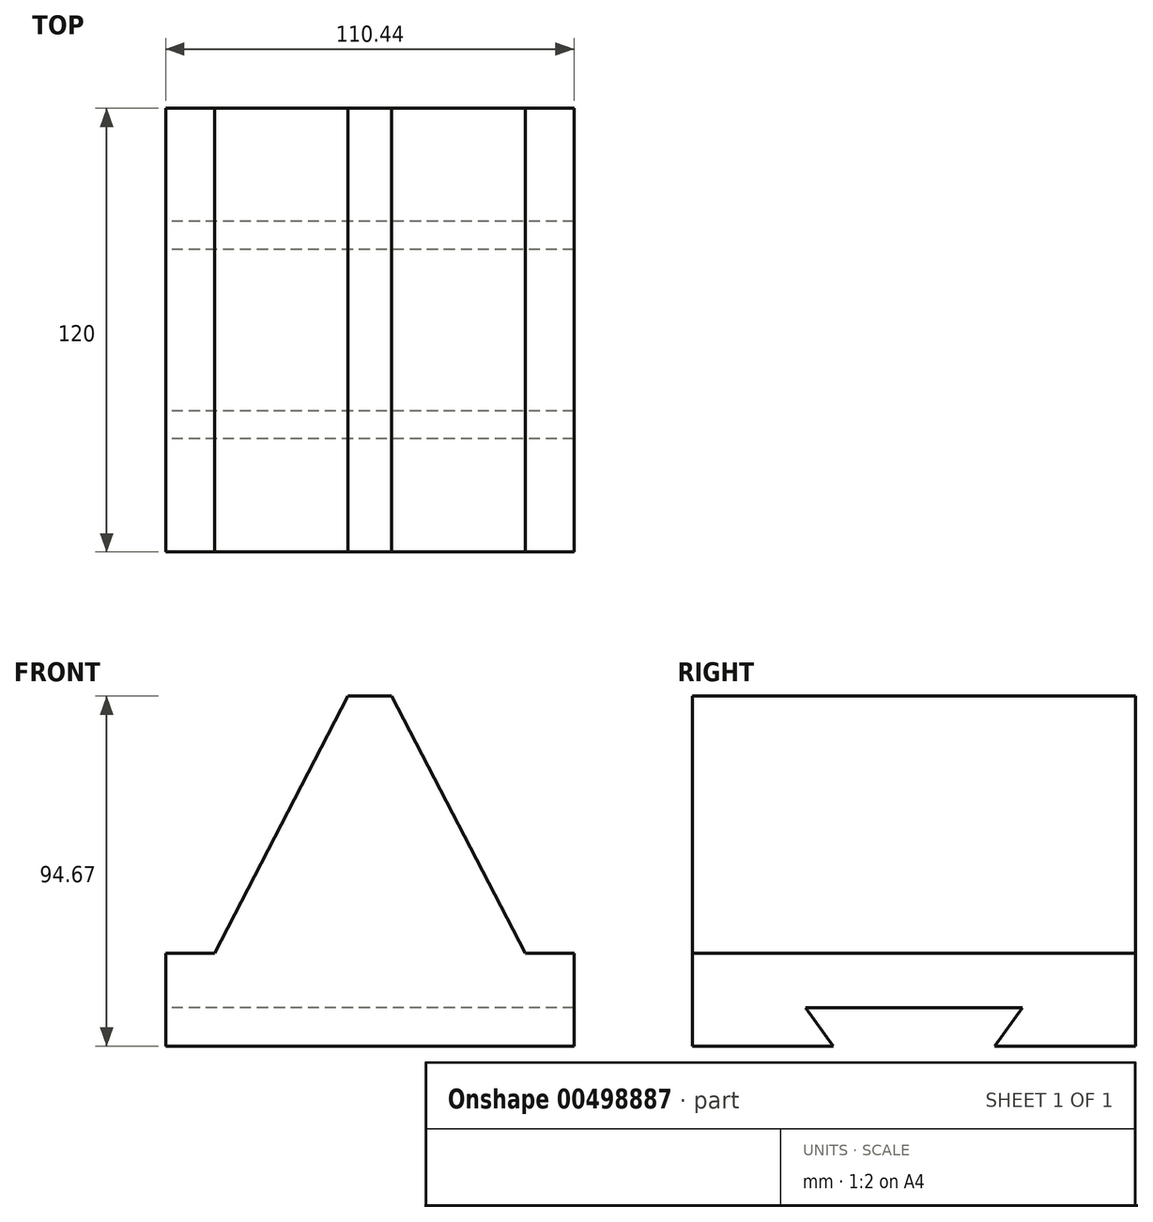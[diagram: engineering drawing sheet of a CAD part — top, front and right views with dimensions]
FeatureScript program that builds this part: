
annotation { "Feature Type Name" : "Feature", "Feature Type Description" : "" }
export const myFeature = defineFeature(function(context is Context, id is Id, definition is map)
    precondition{}
    {
        {
            var Q0;
            Q0=qCreatedBy(makeId("Front.planeOp"),FACE);
            var sketch = newSketch(context, id + "F0", { "sketchPlane" : qUnion([Q0])});
            skLineSegment(sketch, "E0", {"start": v(55.22, 0) * mm, "end": v(-55.22, 0) * mm});
            skLineSegment(sketch, "E1", {"start": v(-55.22, 0) * mm, "end": v(-55.22, 25.1) * mm});
            skLineSegment(sketch, "E2", {"start": v(-55.22, 25.1) * mm, "end": v(-42.05, 25.1) * mm});
            skLineSegment(sketch, "E3", {"start": v(-5.92, 94.67) * mm, "end": v(-42.05, 25.1) * mm});
            skLineSegment(sketch, "E4", {"start": v(-5.92, 94.67) * mm, "end": v(5.92, 94.67) * mm});
            skLineSegment(sketch, "E5", {"start": v(42.05, 25.1) * mm, "end": v(5.92, 94.67) * mm});
            skLineSegment(sketch, "E6", {"start": v(42.05, 25.1) * mm, "end": v(55.22, 25.1) * mm});
            skLineSegment(sketch, "E7", {"start": v(55.22, 25.1) * mm, "end": v(55.22, 0) * mm});
            skLineSegment(sketch, "E8", {"start": v(0, 94.67) * mm, "end": v(0, 0) * mm, "construction": true});
            skSolve(sketch);
        }
        {
            var Q0;
            Q0=makeQuery(id+"F0.imprint","IMPRINT",FACE,{"disambiguationData":[TD([[makeQuery(id+"F0.imprint","IMPRINT",EDGE,{"derivedFrom":sQuery(id+"F0.wireOp",EDGE,"E0")}),-1.0]])]});
            extrude(context, id + "F1", {"entities" : qUnion([Q0]), "endBound" : BoundingType.SYMMETRIC, "depth" : 120 * mm});
        }
        {
            var Q0;
            Q0=makeQuery(id+"F1.opExtrude","SWEPT_FACE",FACE,{"disambiguationData":[OSD([sQuery(id+"F0.wireOp",EDGE,"E1")])]});
            var sketch = newSketch(context, id + "F2", { "sketchPlane" : qUnion([Q0])});
            skLineSegment(sketch, "E9", {"start": v(0, 0) * mm, "end": v(0, 66.65) * mm, "construction": true});
            skPoint(sketch, "E9.endSnap0", {"position": v(0, 0) * mm});
            skLineSegment(sketch, "E10", {"start": v(-21.83, 0) * mm, "end": v(-29.37, 10.37) * mm});
            skLineSegment(sketch, "E11", {"start": v(-29.37, 10.37) * mm, "end": v(29.37, 10.37) * mm});
            skLineSegment(sketch, "E12", {"start": v(29.37, 10.37) * mm, "end": v(21.83, 0) * mm});
            skLineSegment(sketch, "E13", {"start": v(-21.83, 0) * mm, "end": v(21.83, 0) * mm});
            skSolve(sketch);
        }
        {
            var Q0;
            Q0=makeQuery(id+"F2.imprint","IMPRINT",FACE,{"disambiguationData":[TD([[makeQuery(id+"F2.imprint","IMPRINT",EDGE,{"derivedFrom":sQuery(id+"F2.wireOp",EDGE,"E10")}),-1.0]])]});
            extrude(context, id + "F3", {"entities" : qUnion([Q0]), "operationType" : NewBodyOperationType.REMOVE, "endBound" : BoundingType.THROUGH_ALL, "oppositeDirection" : true, "depth" : 25 * mm});
        }
    });
